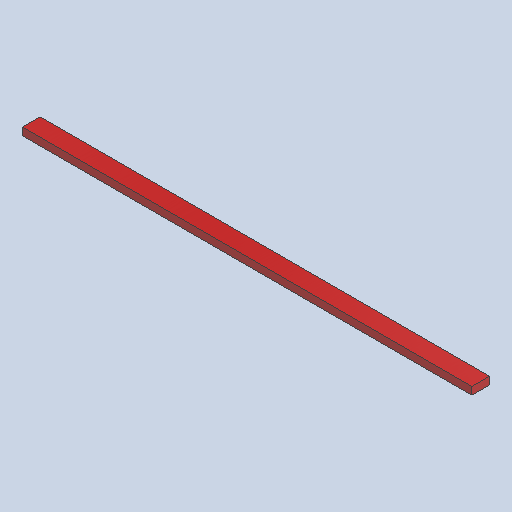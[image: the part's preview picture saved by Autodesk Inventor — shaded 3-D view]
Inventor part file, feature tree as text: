
AUTODESK INVENTOR PART (.ipt)
format: ipt  version: 2025.1 (Build 291241020, 241B)  size: 253,440 bytes
history: native  units: in
note: dims shown in document units (in); Inventor stores cm internally (conversion verified against a paired STEP export)
features: other x2, extrude x1, sketch x1
ambient origin geometry x8: Origin, YZ Plane, XZ Plane, XY Plane, X Axis, Y Axis, Z Axis, Center Point
bodies: Solid1 (feature_tree)
feature tree (4):
  extrude  "Extrusion1"  Depth=1.5in
  sketch  "Sketch1"  dims[d0=3.5in d1=1.5in d2=89.0in d3=0.0in]
  other  "Finish1"
  other  "Finish2"
